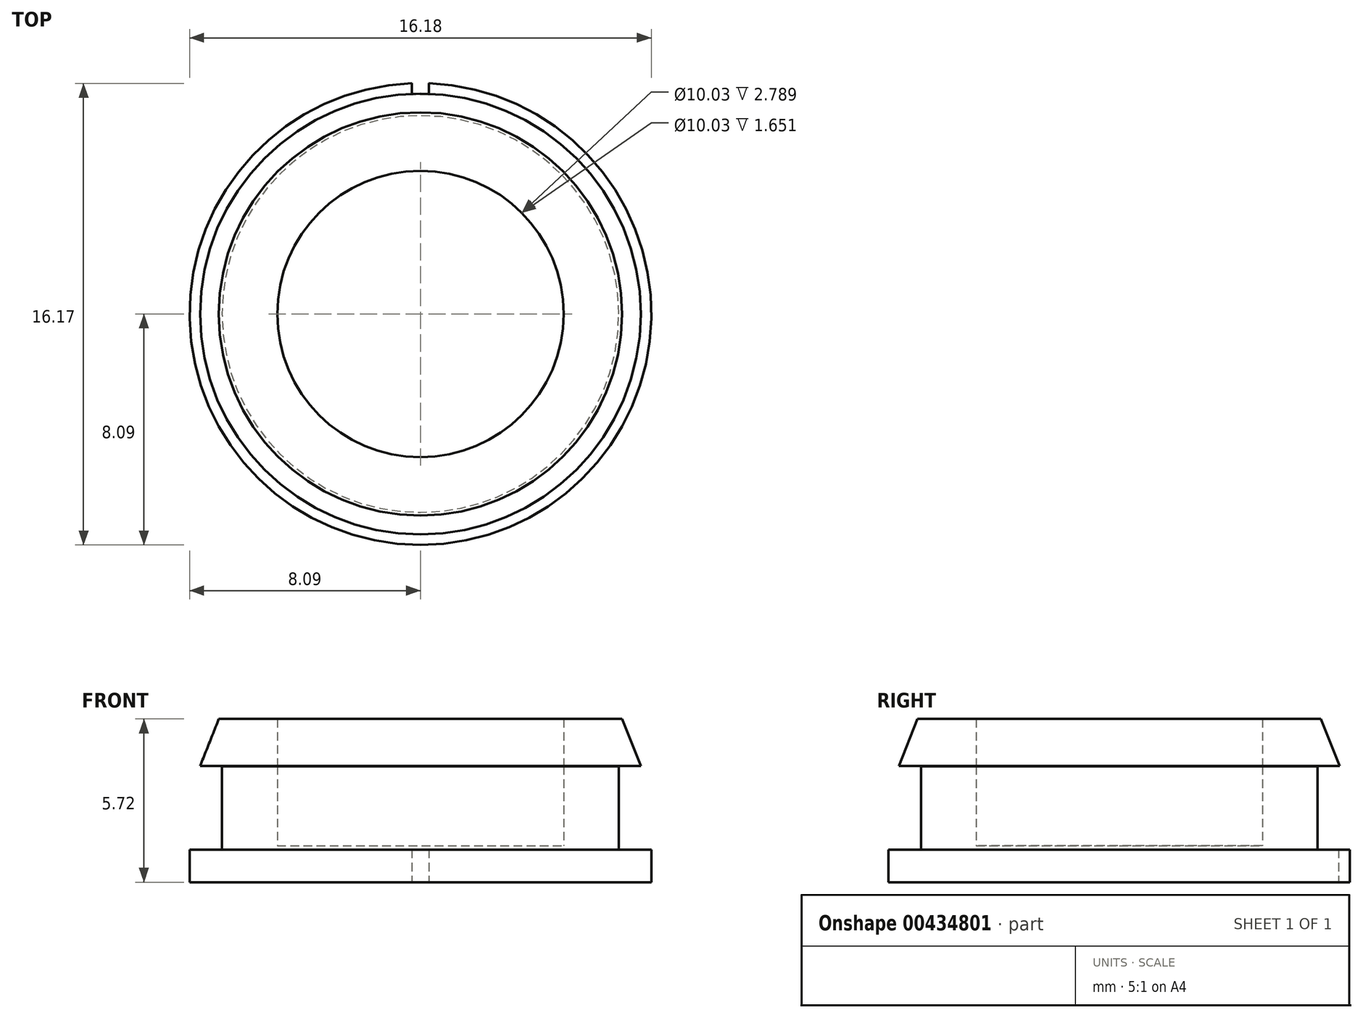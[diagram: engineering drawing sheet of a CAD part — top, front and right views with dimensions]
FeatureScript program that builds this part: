
annotation { "Feature Type Name" : "Feature", "Feature Type Description" : "" }
export const myFeature = defineFeature(function(context is Context, id is Id, definition is map)
    precondition{}
    {
        {
            var Q0;
            Q0=qCreatedBy(makeId("Front.planeOp"),FACE);
            var sketch = newSketch(context, id + "F0", { "sketchPlane" : qUnion([Q0])});
            skLineSegment(sketch, "E0.bottom", {"start": v(-8.09, -0.57) * mm, "end": v(8.09, -0.57) * mm});
            skLineSegment(sketch, "E0.top", {"start": v(-8.09, 0.57) * mm, "end": v(8.09, 0.57) * mm});
            skLineSegment(sketch, "E0.left", {"start": v(-8.09, -0.57) * mm, "end": v(-8.09, 0.57) * mm});
            skLineSegment(sketch, "E0.right", {"start": v(8.09, -0.57) * mm, "end": v(8.09, 0.57) * mm});
            skLineSegment(sketch, "E1.bottom", {"start": v(-7.75, 3.5) * mm, "end": v(7.72, 3.5) * mm});
            skLineSegment(sketch, "E1.top", {"start": v(-7.07, 5.15) * mm, "end": v(7.07, 5.15) * mm});
            skLineSegment(sketch, "E2.bottom", {"start": v(-7, 3.5) * mm, "end": v(6.95, 3.5) * mm});
            skLineSegment(sketch, "E2.top", {"start": v(-7, 0.57) * mm, "end": v(6.95, 0.57) * mm});
            skLineSegment(sketch, "E2.left", {"start": v(-7, 3.5) * mm, "end": v(-7, 0.57) * mm});
            skLineSegment(sketch, "E2.right", {"start": v(6.95, 3.5) * mm, "end": v(6.95, 0.57) * mm});
            skLineSegment(sketch, "E3", {"start": v(0, -0.57) * mm, "end": v(0, 5.15) * mm});
            skPoint(sketch, "E3.endSnap0", {"position": v(0, 0.57) * mm});
            skLineSegment(sketch, "E4", {"start": v(7.72, 3.5) * mm, "end": v(7.07, 5.15) * mm});
            skLineSegment(sketch, "E5", {"start": v(-7.75, 3.5) * mm, "end": v(-7.07, 5.15) * mm});
            skLineSegment(sketch, "E6.bottom", {"start": v(5.02, 0.7) * mm, "end": v(-5.02, 0.7) * mm});
            skLineSegment(sketch, "E6.top", {"start": v(5.02, 5.15) * mm, "end": v(-5.02, 5.15) * mm});
            skLineSegment(sketch, "E6.left", {"start": v(5.02, 0.7) * mm, "end": v(5.02, 5.15) * mm});
            skLineSegment(sketch, "E6.right", {"start": v(-5.02, 0.7) * mm, "end": v(-5.02, 5.15) * mm});
            skPoint(sketch, "E6.middle", {"position": v(0, 2.93) * mm});
            skSolve(sketch);
        }
        {
            var Q0;
            {var subQ0=sQuery(id+"F0.wireOp",EDGE,"E4");Q0=makeQuery(id+"F0.imprint","IMPRINT",FACE,{"disambiguationData":[TD([[makeQuery(id+"F0.imprint","IMPRINT",EDGE,{"derivedFrom":subQ0}),1.0]])]});}
            var Q1;
            {var subQ0=sQuery(id+"F0.wireOp",EDGE,"E2.right");Q1=makeQuery(id+"F0.imprint","IMPRINT",FACE,{"disambiguationData":[TD([[makeQuery(id+"F0.imprint","IMPRINT",EDGE,{"derivedFrom":subQ0}),-1.0]])]});}
            var Q2;
            {var subQ0=sQuery(id+"F0.wireOp",EDGE,"E0.right");Q2=makeQuery(id+"F0.imprint","IMPRINT",FACE,{"disambiguationData":[TD([[makeQuery(id+"F0.imprint","IMPRINT",EDGE,{"derivedFrom":subQ0}),1.0]])]});}
            var Q3;
            Q3=sQuery(id+"F0.wireOp",EDGE,"E3");
            revolve(context, id + "F1", {"entities" : qUnion([Q0, Q1, Q2]), "axis" : qUnion([Q3]), "revolveType" : RevolveType.FULL});
        }
        {
            var Q0;
            {var subQ0=sQuery(id+"F0.wireOp",EDGE,"E6.right");var subQ1=sQuery(id+"F0.wireOp",EDGE,"E2.bottom");var subQ2=makeQuery(id+"F0.imprint","INTERSECT",VERTEX,{"derivedFrom":[subQ1,subQ0]});Q0=makeQuery(id+"F0.imprint","IMPRINT",FACE,{"disambiguationData":[TD([[makeQuery(id+"F0.imprint","IMPRINT",EDGE,{"disambiguationData":[TD([[subQ2,-1.0]])],"derivedFrom":subQ1}),-1.0]])]});}
            var Q1;
            Q1=sQuery(id+"F0.wireOp",EDGE,"E3");
            revolve(context, id + "F2", {"operationType" : NewBodyOperationType.REMOVE, "entities" : qUnion([Q0]), "axis" : qUnion([Q1]), "revolveType" : RevolveType.FULL, "oppositeDirection" : true});
        }
        {
            var Q0;
            Q0=qCreatedBy(makeId("Top.planeOp"),FACE);
            var sketch = newSketch(context, id + "F3", { "sketchPlane" : qUnion([Q0])});
            skLineSegment(sketch, "E7.bottom", {"start": v(0.3, 8.1) * mm, "end": v(-0.3, 8.1) * mm});
            skLineSegment(sketch, "E7.top", {"start": v(0.3, 7.69) * mm, "end": v(-0.3, 7.69) * mm});
            skLineSegment(sketch, "E7.left", {"start": v(0.3, 8.1) * mm, "end": v(0.3, 7.69) * mm});
            skLineSegment(sketch, "E7.right", {"start": v(-0.3, 8.1) * mm, "end": v(-0.3, 7.69) * mm});
            skLineSegment(sketch, "E8.bottom", {"start": v(0, 7.9) * mm, "end": v(0, 7.9) * mm});
            skLineSegment(sketch, "E8.top", {"start": v(0, 7.7) * mm, "end": v(0, 7.7) * mm});
            skSolve(sketch);
        }
        {
            var Q0;
            Q0 = qSketchRegion(id + "F3", true);
            extrude(context, id + "F4", {"entities" : qUnion([Q0]), "operationType" : NewBodyOperationType.REMOVE, "endBound" : BoundingType.SYMMETRIC, "depth" : 6.35 * mm});
        }
    });
